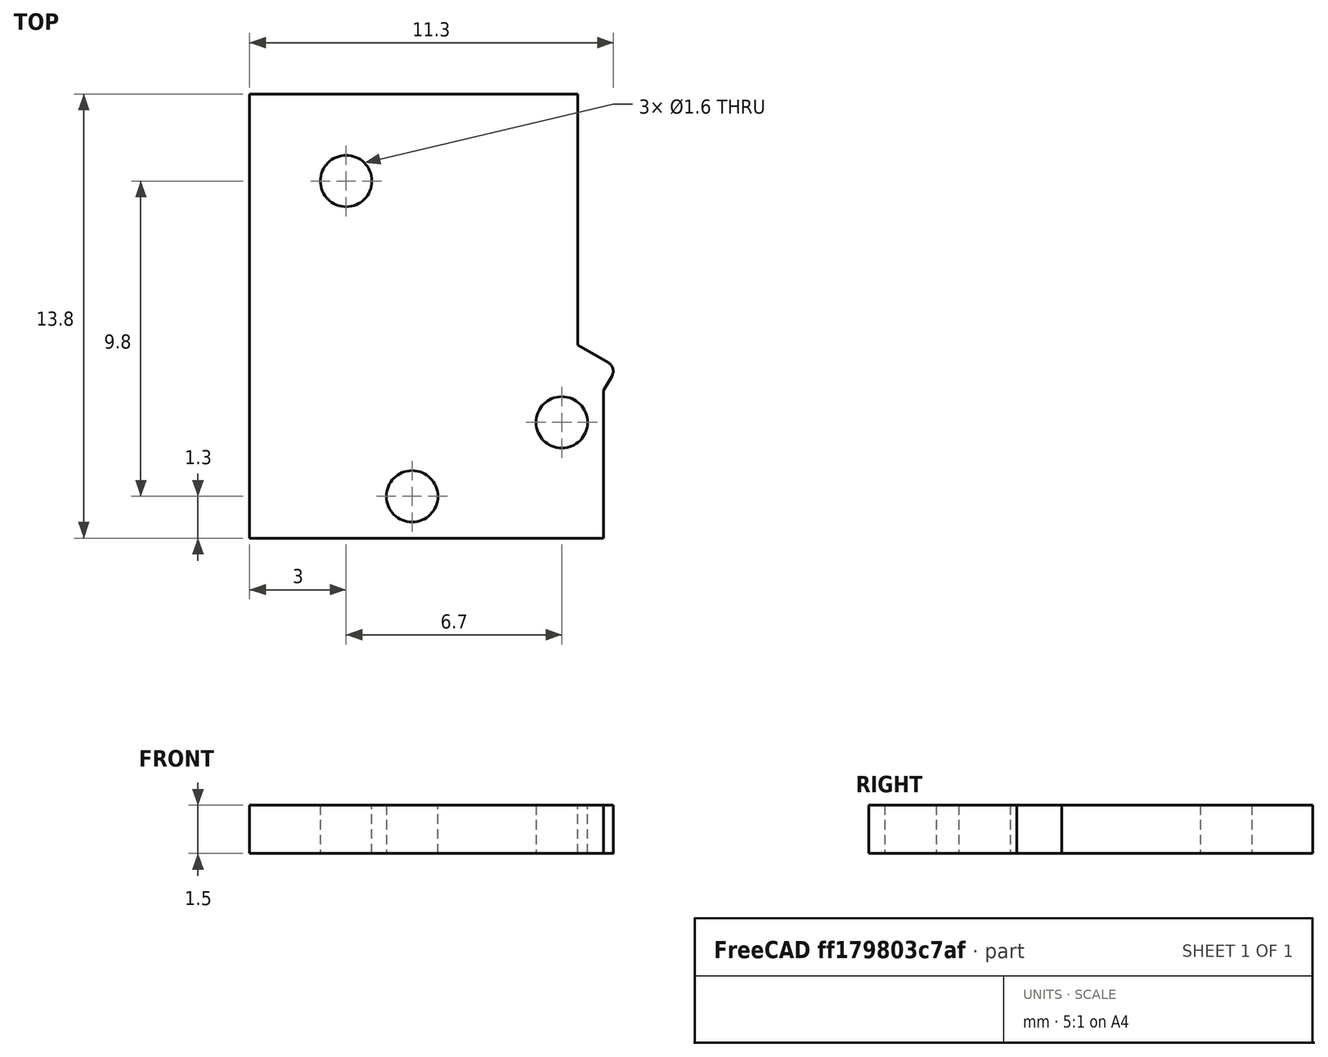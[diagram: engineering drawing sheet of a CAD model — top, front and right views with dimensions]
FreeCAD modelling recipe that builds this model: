
FCSTD DOCUMENT  (FreeCAD 1.0R38641 +678 (Git))
Label: cover
License: All rights reserved
LicenseURL: https://en.wikipedia.org/wiki/All_rights_reserved
objects: Image::ImagePlane×2, Sketcher::SketchObject×1, PartDesign::Pad×1, PartDesign::Body×1
note: 6 computed .brp shape members not serialized (recipe doc carries the construction recipe); baked Part::Feature solids carry a one-line shape summary decoded from their .brp

FEATURE [Image::ImagePlane] KF141R
  Placement = pos=(2.4,5.6,0) rot=(0,0,1;-1.5708rad)
  XSize = 23.0527
  YSize = 24.858
FEATURE [Image::ImagePlane] KF141V
  Placement = pos=(6.1,3.9,0) rot=(0,0,1;0rad)
  XSize = 20.4337
  YSize = 24.1373
FEATURE [Sketcher::SketchObject] Sketch
  ArcFitTolerance = 1e-06
  AttachmentSupport = -> [XY_Plane001]
  FullyConstrained = true
  MakeInternals = false
  MapMode = 5
  sketch-geometry (11):
    g0: LineSegment StartX=0 StartY=0 StartZ=0 EndX=11 EndY=0 EndZ=0
    g1: LineSegment StartX=11 StartY=0 StartZ=0 EndX=11 EndY=4.6 EndZ=0
    g2: LineSegment StartX=11 StartY=4.6 StartZ=0 EndX=11.2562 EndY=5.04378 EndZ=0
    g3: ArcOfCircle CenterX=10.9964 CenterY=5.19378 CenterZ=0 NormalX=0 NormalY=0 NormalZ=1 AngleXU=0 Radius=0.3 StartAngle=5.75959 EndAngle=7.33038
    g4: LineSegment StartX=11.1464 StartY=5.45359 StartZ=0 EndX=10.2 EndY=6 EndZ=0
    g5: LineSegment StartX=10.2 StartY=6 StartZ=0 EndX=10.2 EndY=13.8 EndZ=0
    g6: LineSegment StartX=10.2 StartY=13.8 StartZ=0 EndX=0 EndY=13.8 EndZ=0
    g7: LineSegment StartX=0 StartY=13.8 StartZ=0 EndX=0 EndY=0 EndZ=0
    g8: Circle CenterX=5.05 CenterY=1.3 CenterZ=0 NormalX=0 NormalY=0 NormalZ=1 AngleXU=0 Radius=0.8
    g9: Circle CenterX=9.7 CenterY=3.6 CenterZ=0 NormalX=0 NormalY=0 NormalZ=1 AngleXU=0 Radius=0.8
    g10: Circle CenterX=3 CenterY=11.1 CenterZ=0 NormalX=0 NormalY=0 NormalZ=1 AngleXU=0 Radius=0.8
  constraints (31):
    c: Coincident(g-1,g0)
    c: PointOnObject(g0,g-1)
    c: Coincident(g0,g1)
    c: Vertical(g1)
    c: Coincident(g1,g2)
    c: Tangent(g2,g3) = -1.5708
    c: Tangent(g3,g4) = -1.5708
    c: Coincident(g4,g5)
    c: Vertical(g5)
    c: Coincident(g5,g6)
    c: PointOnObject(g6,g-2)
    c: Horizontal(g6)
    c: Coincident(g6,g7)
    c: Coincident(g7,g0)
    c: DistanceX(g0,g0) = 11
    c: DistanceY(g7,g7) = 13.8
    c: DistanceX(g6,g6) = 10.2
    c: DistanceY(g5,g5) = 7.8
    c: DistanceY(g1,g1) = 4.6
    c: Radius(g3) = 0.3
    c: Angle(g1,g2) = 2.61799
    c: Angle(g4,g5) = 2.0944
    c: Equal(g10,g8)
    c: Equal(g8,g9)
    c: Diameter(g10) = 1.6
    c: DistanceX(g-1,g8) = 5.05
    c: DistanceY(g-1,g8) = 1.3
    c: DistanceY(g-1,g9) = 3.6
    c: DistanceX(g-1,g9) = 9.7
    c: DistanceY(g-1,g10) = 11.1
    c: DistanceX(g-1,g10) = 3
FEATURE [PartDesign::Pad] Pad
  Direction = (0,0,1)
  Length = 1.5
  Length2 = 10
  Profile = -> Sketch
  ReferenceAxis = -> Sketch [N_Axis]
  Refine = true
  Suppressed = false
  Type = 0
FEATURE [PartDesign::Body] Body001  label="Cover"
  AllowCompound = false
  Group = -> [Sketch,Pad]
  Origin = -> Origin001
  Tip = -> Pad
